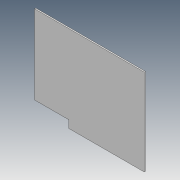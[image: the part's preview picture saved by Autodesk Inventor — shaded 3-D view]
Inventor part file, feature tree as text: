
AUTODESK INVENTOR PART (.ipt)
format: ipt  version: 2021 (Build 250183000, 183)  size: 94,208 bytes
history: native  units: in
note: dims shown in document units (in); Inventor stores cm internally (conversion verified against a paired STEP export)
features: extrude x3, sketch x3, other x1
ambient origin geometry x8: Origin, YZ Plane, XZ Plane, XY Plane, X Axis, Y Axis, Z Axis, Center Point
bodies: Body1 (feature_tree)
feature tree (7):
  other  "Sólido1"
  extrude  "Extrusão1"  Depth=1.2362in
  extrude  "Extrusão2"  Depth=0.0197in
  extrude  "Extrusão3"  Depth=1.1811in
  sketch  "Esboço1"  dims[d0=1.9685in d1=1.2362in]
  sketch  "Esboço2"  dims[d2=0.0197in d3=0.0in d4=0.252in]
  sketch  "Esboço3"  dims[d5=0.0197in d6=0.0in d7=1.1811in d8=0.1181in d9=0.0197in d10=0.0in]
